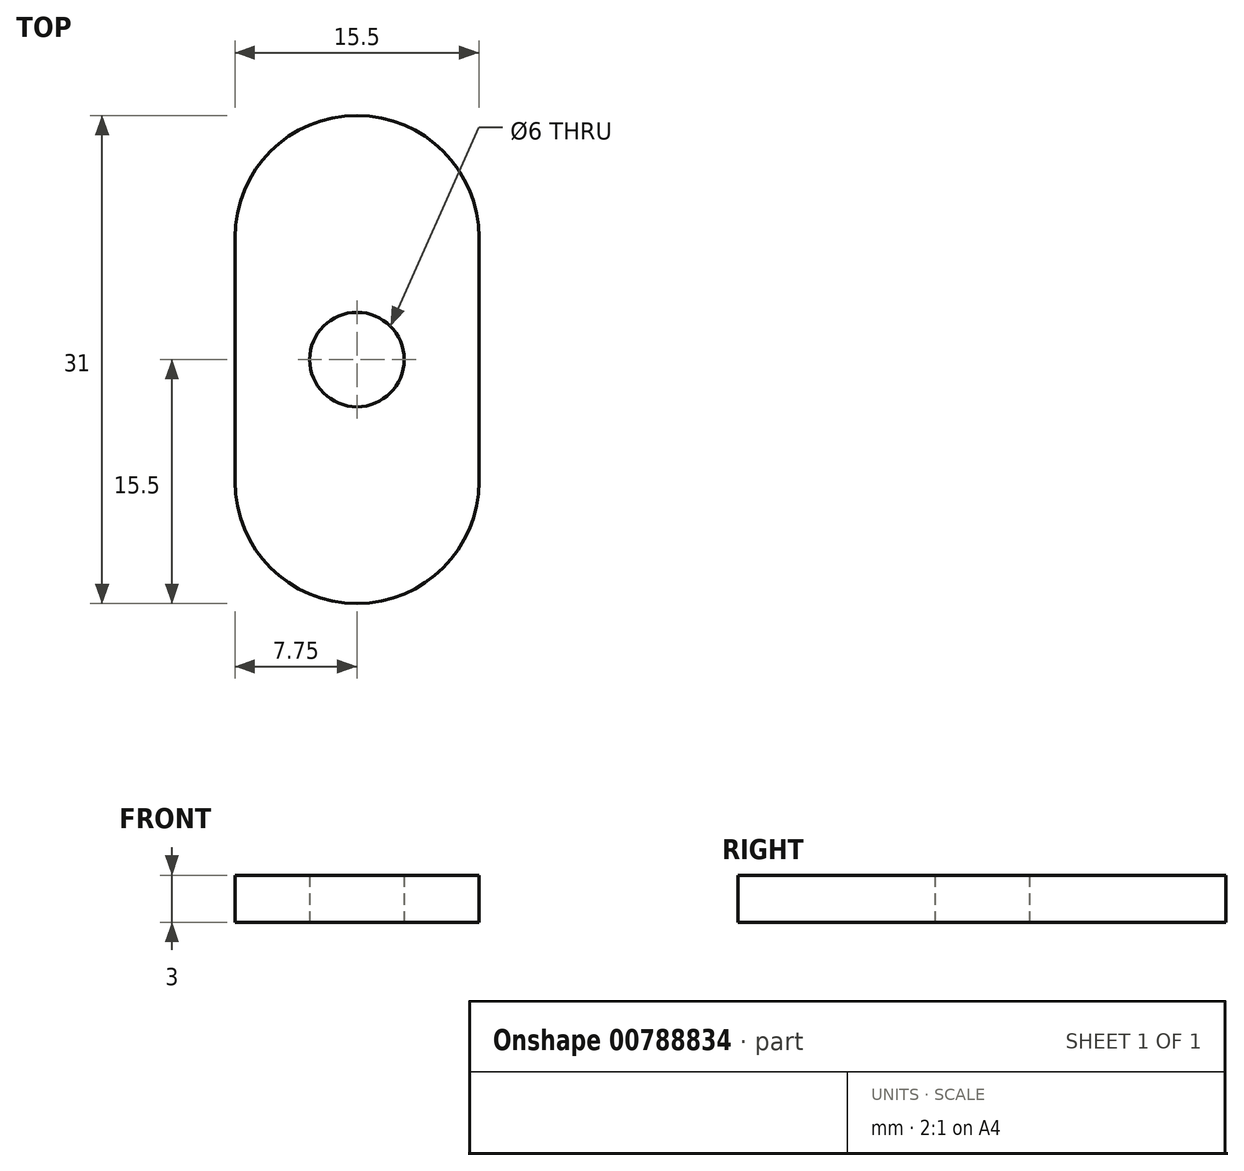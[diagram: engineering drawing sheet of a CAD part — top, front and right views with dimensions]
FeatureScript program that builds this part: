
annotation { "Feature Type Name" : "Feature", "Feature Type Description" : "" }
export const myFeature = defineFeature(function(context is Context, id is Id, definition is map)
    precondition{}
    {
        {
            var Q0;
            Q0=qCreatedBy(makeId("Top.planeOp"),FACE);
            var sketch = newSketch(context, id + "F0", { "sketchPlane" : qUnion([Q0])});
            skLineSegment(sketch, "E0.left", {"start": v(7.75, -7.75) * mm, "end": v(7.75, 7.75) * mm});
            skLineSegment(sketch, "E0.right", {"start": v(-7.75, -7.75) * mm, "end": v(-7.75, 7.75) * mm});
            skPoint(sketch, "E0.middle", {"position": v(0, 0) * mm});
            skArc(sketch, "E1", {"start": v(7.75, 7.75) * mm, "mid": v(0, 15.5) * mm, "end": v(-7.75, 7.75) * mm});
            skArc(sketch, "E2", {"start": v(-7.75, -7.75) * mm, "mid": v(0, -15.5) * mm, "end": v(7.75, -7.75) * mm});
            skCircle(sketch, "E3", {"center": v(0, 0) * mm, "radius": 3 * mm});
            skSolve(sketch);
        }
        {
            var Q0;
            Q0=makeQuery(id+"F0.imprint","IMPRINT",FACE,{"disambiguationData":[TD([[makeQuery(id+"F0.imprint","IMPRINT",EDGE,{"derivedFrom":sQuery(id+"F0.wireOp",EDGE,"E0.left")}),1.0]])]});
            extrude(context, id + "F1", {"entities" : qUnion([Q0]), "depth" : 3 * mm, "offsetDistance" : 25 * mm});
        }
    });
